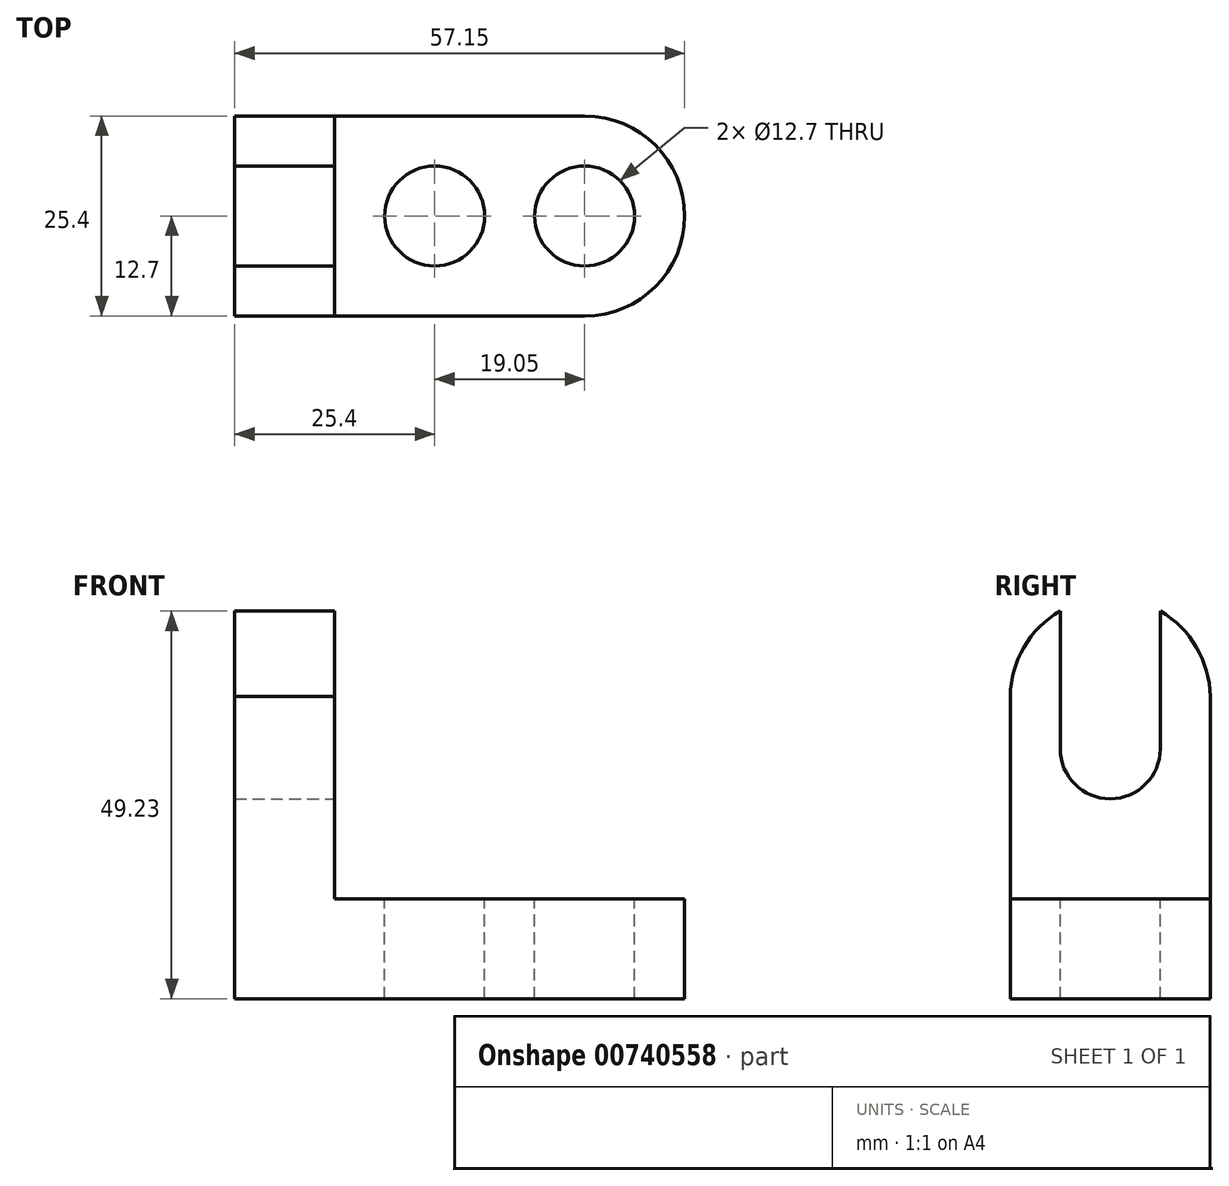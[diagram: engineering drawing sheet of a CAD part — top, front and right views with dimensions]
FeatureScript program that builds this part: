
annotation { "Feature Type Name" : "Feature", "Feature Type Description" : "" }
export const myFeature = defineFeature(function(context is Context, id is Id, definition is map)
    precondition{}
    {
        {
            var Q0;
            Q0=qCreatedBy(makeId("Front.planeOp"),FACE);
            var sketch = newSketch(context, id + "F0", { "sketchPlane" : qUnion([Q0])});
            skLineSegment(sketch, "E0", {"start": v(0, 0) * mm, "end": v(57.15, 0) * mm});
            skLineSegment(sketch, "E1", {"start": v(57.15, 0) * mm, "end": v(57.15, 12.7) * mm});
            skLineSegment(sketch, "E2", {"start": v(57.15, 12.7) * mm, "end": v(12.7, 12.7) * mm});
            skLineSegment(sketch, "E3", {"start": v(12.7, 12.7) * mm, "end": v(12.7, 50.8) * mm});
            skLineSegment(sketch, "E4", {"start": v(12.7, 50.8) * mm, "end": v(0, 50.8) * mm});
            skLineSegment(sketch, "E5", {"start": v(0, 50.8) * mm, "end": v(0, 0) * mm});
            skSolve(sketch);
        }
        {
            var Q0;
            Q0 = qSketchRegion(id + "F0", true);
            extrude(context, id + "F1", {"entities" : qUnion([Q0]), "depth" : 25.4 * mm, "offsetDistance" : 25.4 * mm});
        }
        {
            var Q0;
            Q0=makeQuery(id+"F1.opExtrude","SWEPT_FACE",FACE,{"disambiguationData":[OSD([sQuery(id+"F0.wireOp",EDGE,"E3")])]});
            var sketch = newSketch(context, id + "F2", { "sketchPlane" : qUnion([Q0])});
            skLineSegment(sketch, "E6", {"start": v(-25.4, 31.75) * mm, "end": v(0, 31.75) * mm});
            skCircle(sketch, "E7", {"center": v(-12.7, 31.75) * mm, "radius": 6.35 * mm});
            skLineSegment(sketch, "E8", {"start": v(-6.35, 31.75) * mm, "end": v(-6.35, 50.8) * mm});
            skLineSegment(sketch, "E9", {"start": v(-19.05, 31.75) * mm, "end": v(-19.05, 50.8) * mm});
            skSolve(sketch);
        }
        {
            var Q0;
            Q0 = qSketchRegion(id + "F2", true);
            var Q1;
            {var subQ0=sQuery(id+"F2.wireOp",EDGE,"E8");Q1=makeQuery(id+"F2.imprint","IMPRINT",FACE,{"disambiguationData":[TD([[makeQuery(id+"F2.imprint","IMPRINT",EDGE,{"derivedFrom":subQ0}),1.0]])]});}
            extrude(context, id + "F3", {"entities" : qUnion([Q0, Q1]), "operationType" : NewBodyOperationType.REMOVE, "endBound" : BoundingType.THROUGH_ALL, "oppositeDirection" : true, "depth" : 25.4 * mm, "offsetDistance" : 25.4 * mm});
        }
        {
            var Q0;
            Q0=makeQuery(id+"F1.opExtrude","SWEPT_FACE",FACE,{"disambiguationData":[OSD([sQuery(id+"F0.wireOp",EDGE,"E3")])]});
            var sketch = newSketch(context, id + "F4", { "sketchPlane" : qUnion([Q0])});
            skLineSegment(sketch, "E10", {"start": v(-25.4, 38.1) * mm, "end": v(0, 38.1) * mm});
            skArc(sketch, "E11", {"start": v(0, 38.1) * mm, "mid": v(-12.7, 50.93) * mm, "end": v(-25.4, 38.1) * mm});
            skSolve(sketch);
        }
        {
            var Q0;
            {var subQ0=sQuery(id+"F4.wireOp",EDGE,"E11");var subQ1=sQuery(id+"F2.wireOp",EDGE,"E9");var subQ2=makeQuery(id+"F3.boolean.opBoolean","COPY",EDGE,{"derivedFrom":makeQuery(id+"F3.opExtrude","CAP_EDGE",EDGE,{"disambiguationData":[OSD([subQ1])],"isStart":true})});var subQ3=makeQuery(id+"F4.imprint","INTERSECT",VERTEX,{"derivedFrom":[subQ2,subQ0]});Q0=makeQuery(id+"F4.imprint","IMPRINT",FACE,{"disambiguationData":[TD([[makeQuery(id+"F4.imprint","IMPRINT",EDGE,{"disambiguationData":[TD([[subQ3,-1.0]])],"derivedFrom":subQ0}),-1.0]])]});}
            var Q1;
            {var subQ0=sQuery(id+"F4.wireOp",EDGE,"E11");var subQ1=sQuery(id+"F0.wireOp",EDGE,"E3");var subQ2=makeQuery(id+"F1.opExtrude","CAP_EDGE",EDGE,{"disambiguationData":[OSD([subQ1])],"isStart":true});var subQ3=makeQuery(id+"F4.imprint","INTERSECT",VERTEX,{"derivedFrom":[subQ2,subQ0]});Q1=makeQuery(id+"F4.imprint","IMPRINT",FACE,{"disambiguationData":[TD([[makeQuery(id+"F4.imprint","IMPRINT",EDGE,{"disambiguationData":[TD([[subQ3,-1.0]])],"derivedFrom":subQ0}),-1.0]])]});}
            extrude(context, id + "F5", {"entities" : qUnion([Q0, Q1]), "operationType" : NewBodyOperationType.REMOVE, "endBound" : BoundingType.THROUGH_ALL, "oppositeDirection" : true, "depth" : 25.4 * mm, "offsetDistance" : 25.4 * mm});
        }
        {
            var Q0;
            Q0=makeQuery(id+"F1.opExtrude","SWEPT_FACE",FACE,{"disambiguationData":[OSD([sQuery(id+"F0.wireOp",EDGE,"E2")])]});
            var sketch = newSketch(context, id + "F6", { "sketchPlane" : qUnion([Q0])});
            skLineSegment(sketch, "E12", {"start": v(25.4, -25.4) * mm, "end": v(25.4, 0) * mm});
            skLineSegment(sketch, "E13", {"start": v(25.4, 0) * mm, "end": v(44.45, 0) * mm});
            skLineSegment(sketch, "E14", {"start": v(44.45, 0) * mm, "end": v(44.45, -25.4) * mm});
            skCircle(sketch, "E15", {"center": v(25.4, -12.7) * mm, "radius": 6.35 * mm});
            skCircle(sketch, "E16", {"center": v(44.45, -12.7) * mm, "radius": 6.35 * mm});
            skArc(sketch, "E17", {"start": v(44.45, -25.4) * mm, "mid": v(57.15, -12.7) * mm, "end": v(44.45, 0) * mm});
            skSolve(sketch);
        }
        {
            var Q0;
            {var subQ0=sQuery(id+"F6.wireOp",EDGE,"E15");var subQ1=sQuery(id+"F6.wireOp",EDGE,"E12");var subQ2=makeQuery(id+"F6.imprint","INTERSECT",VERTEX,{"disambiguationData":[OD(0.0)],"derivedFrom":[subQ1,subQ0]});Q0=makeQuery(id+"F6.imprint","IMPRINT",FACE,{"disambiguationData":[TD([[makeQuery(id+"F6.imprint","IMPRINT",EDGE,{"disambiguationData":[TD([[subQ2,-1.0]])],"derivedFrom":subQ1}),1.0]])]});}
            var Q1;
            {var subQ0=sQuery(id+"F6.wireOp",EDGE,"E15");var subQ1=sQuery(id+"F6.wireOp",EDGE,"E12");var subQ2=makeQuery(id+"F6.imprint","INTERSECT",VERTEX,{"disambiguationData":[OD(0.0)],"derivedFrom":[subQ1,subQ0]});Q1=makeQuery(id+"F6.imprint","IMPRINT",FACE,{"disambiguationData":[TD([[makeQuery(id+"F6.imprint","IMPRINT",EDGE,{"disambiguationData":[TD([[subQ2,-1.0]])],"derivedFrom":subQ1}),-1.0]])]});}
            var Q2;
            {var subQ0=sQuery(id+"F6.wireOp",EDGE,"E16");var subQ1=sQuery(id+"F6.wireOp",EDGE,"E14");var subQ2=makeQuery(id+"F6.imprint","INTERSECT",VERTEX,{"disambiguationData":[OD(0.0)],"derivedFrom":[subQ1,subQ0]});Q2=makeQuery(id+"F6.imprint","IMPRINT",FACE,{"disambiguationData":[TD([[makeQuery(id+"F6.imprint","IMPRINT",EDGE,{"disambiguationData":[TD([[subQ2,-1.0]])],"derivedFrom":subQ1}),-1.0]])]});}
            var Q3;
            {var subQ0=sQuery(id+"F6.wireOp",EDGE,"E16");var subQ1=sQuery(id+"F6.wireOp",EDGE,"E14");var subQ2=makeQuery(id+"F6.imprint","INTERSECT",VERTEX,{"disambiguationData":[OD(0.0)],"derivedFrom":[subQ1,subQ0]});Q3=makeQuery(id+"F6.imprint","IMPRINT",FACE,{"disambiguationData":[TD([[makeQuery(id+"F6.imprint","IMPRINT",EDGE,{"disambiguationData":[TD([[subQ2,-1.0]])],"derivedFrom":subQ1}),1.0]])]});}
            var Q4;
            {var subQ0=sQuery(id+"F6.wireOp",EDGE,"E17");var subQ1=sQuery(id+"F0.wireOp",EDGE,"E2");var subQ2=makeQuery(id+"F1.opExtrude","CAP_EDGE",EDGE,{"disambiguationData":[OSD([subQ1])],"isStart":false});var subQ3=makeQuery(id+"F6.imprint","INTERSECT",VERTEX,{"derivedFrom":[subQ2,sQuery(id+"F6.wireOp",EDGE,"E14"),subQ0]});Q4=makeQuery(id+"F6.imprint","IMPRINT",FACE,{"disambiguationData":[TD([[makeQuery(id+"F6.imprint","IMPRINT",EDGE,{"disambiguationData":[TD([[subQ3,-1.0]])],"derivedFrom":subQ0}),-1.0]])]});}
            var Q5;
            {var subQ0=sQuery(id+"F6.wireOp",EDGE,"E17");var subQ1=sQuery(id+"F0.wireOp",EDGE,"E2");var subQ4=makeQuery(id+"F1.opExtrude","SWEPT_EDGE",EDGE,{"disambiguationData":[OSD([sQuery(id+"F0.wireOp",EDGE,"E1"),subQ1])]});var subQ5=makeQuery(id+"F6.imprint","INTERSECT",VERTEX,{"derivedFrom":[subQ4,subQ0]});Q5=makeQuery(id+"F6.imprint","IMPRINT",FACE,{"disambiguationData":[TD([[makeQuery(id+"F6.imprint","IMPRINT",EDGE,{"disambiguationData":[TD([[subQ5,-1.0]])],"derivedFrom":subQ0}),-1.0]])]});}
            extrude(context, id + "F7", {"entities" : qUnion([Q0, Q1, Q2, Q3, Q4, Q5]), "operationType" : NewBodyOperationType.REMOVE, "endBound" : BoundingType.THROUGH_ALL, "oppositeDirection" : true, "depth" : 25.4 * mm, "offsetDistance" : 25.4 * mm});
        }
    });
